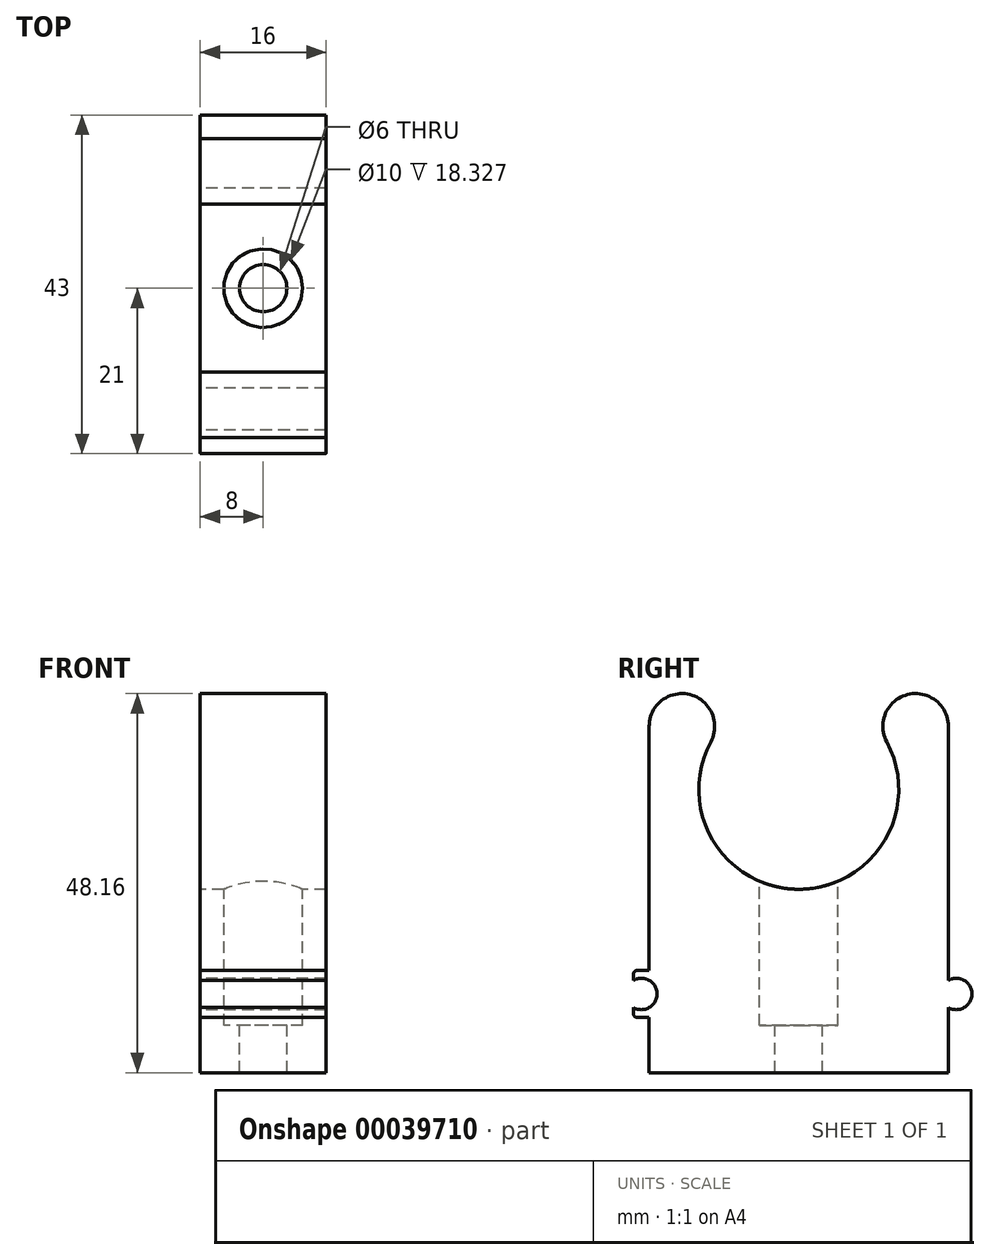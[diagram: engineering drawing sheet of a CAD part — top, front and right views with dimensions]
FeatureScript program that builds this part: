
annotation { "Feature Type Name" : "Feature", "Feature Type Description" : "" }
export const myFeature = defineFeature(function(context is Context, id is Id, definition is map)
    precondition{}
    {
        {
            var Q0;
            Q0=qCreatedBy(makeId("Right.planeOp"),FACE);
            var sketch = newSketch(context, id + "F0", { "sketchPlane" : qUnion([Q0])});
            skLineSegment(sketch, "E0", {"start": v(-19, -36) * mm, "end": v(19, -36) * mm});
            skLineSegment(sketch, "E1", {"start": v(-19, 8) * mm, "end": v(-19, -23) * mm});
            skLineSegment(sketch, "E2", {"start": v(19, -36) * mm, "end": v(19, -27.73) * mm});
            skLineSegment(sketch, "E3", {"start": v(19, -24.27) * mm, "end": v(19, -16.2) * mm});
            skLineSegment(sketch, "E4", {"start": v(19, -16.2) * mm, "end": v(19, 8) * mm});
            skArc(sketch, "E5", {"start": v(-11.18, 6.03) * mm, "mid": v(0, -12.7) * mm, "end": v(11.18, 6.03) * mm});
            skArc(sketch, "E6", {"start": v(-11.18, 6.03) * mm, "mid": v(-13.82, 12.03) * mm, "end": v(-19, 8) * mm});
            skArc(sketch, "E7", {"start": v(19, 8) * mm, "mid": v(13.82, 12.03) * mm, "end": v(11.18, 6.03) * mm});
            skArc(sketch, "E8", {"start": v(19, -27.73) * mm, "mid": v(22, -26) * mm, "end": v(19, -24.27) * mm});
            skArc(sketch, "E9", {"start": v(-21, -27.73) * mm, "mid": v(-18, -26) * mm, "end": v(-21, -24.27) * mm});
            skLineSegment(sketch, "E10", {"start": v(-19, -36) * mm, "end": v(-19, -29) * mm});
            skLineSegment(sketch, "E11", {"start": v(-19, -29) * mm, "end": v(-21, -29) * mm});
            skLineSegment(sketch, "E12", {"start": v(-19, -23) * mm, "end": v(-21, -23) * mm});
            skLineSegment(sketch, "E13", {"start": v(-21, -23) * mm, "end": v(-21, -24.27) * mm});
            skLineSegment(sketch, "E14.trimOffspring", {"start": v(-21, -27.73) * mm, "end": v(-21, -29) * mm});
            skSolve(sketch);
        }
        {
            var Q0;
            Q0=makeQuery(id+"F0.imprint","IMPRINT",FACE,{"disambiguationData":[TD([[makeQuery(id+"F0.imprint","IMPRINT",EDGE,{"derivedFrom":sQuery(id+"F0.wireOp",EDGE,"E0")}),1.0]])]});
            extrude(context, id + "F1", {"entities" : qUnion([Q0]), "depth" : 8 * mm, "hasSecondDirection" : true, "secondDirectionOppositeDirection" : true, "secondDirectionDepth" : 8 * mm});
        }
        {
            var Q0;
            Q0=qCreatedBy(makeId("Top.planeOp"),FACE);
            var sketch = newSketch(context, id + "F2", { "sketchPlane" : qUnion([Q0])});
            skPoint(sketch, "E15", {"position": v(0, 0) * mm});
            skSolve(sketch);
        }
        {
            var Q0;
            Q0=sQuery(id+"F2.wireOp",VERTEX,"E15");
            var Q1;
            Q1=makeQuery(id+"F1.opExtrude","SWEPT_BODY",BODY,{"disambiguationData":[OSD([sQuery(id+"F0.wireOp",EDGE,"E0"),sQuery(id+"F0.wireOp",EDGE,"E1"),sQuery(id+"F0.wireOp",EDGE,"19a90b0d-b803-49e8-be4d-187521ffc359"),sQuery(id+"F0.wireOp",EDGE,"1b800cd7-7c4f-49d2-8106-a57427bceeb3"),sQuery(id+"F0.wireOp",EDGE,"E2"),sQuery(id+"F0.wireOp",EDGE,"E3"),sQuery(id+"F0.wireOp",EDGE,"E4"),sQuery(id+"F0.wireOp",EDGE,"E5"),sQuery(id+"F0.wireOp",EDGE,"E6"),sQuery(id+"F0.wireOp",EDGE,"E7"),sQuery(id+"F0.wireOp",EDGE,"2815f36b-3cf0-4143-92a6-0daac1c242e2"),sQuery(id+"F0.wireOp",EDGE,"1d684afa-b3c8-4d1a-add7-a196b7715977.trimOffspring"),sQuery(id+"F0.wireOp",EDGE,"E8"),sQuery(id+"F0.wireOp",EDGE,"f289f422-6954-4b73-9159-115b672b6794.trimOffspring")])]});
            hole(context, id + "F3", {"style" : HoleStyle.C_BORE, "holeDiameter" : 6 * mm, "cBoreDiameter" : 10 * mm, "cBoreDepth" : 17.3 * mm, "endStyle" : HoleEndStyle.THROUGH, "locations" : qUnion([Q0]), "scope" : qUnion([Q1])});
        }
        {
            var Q0;
            Q0=makeQuery(id+"F1.opExtrude","SWEPT_EDGE",EDGE,{"disambiguationData":[OSD([sQuery(id+"F0.wireOp",EDGE,"E12"),sQuery(id+"F0.wireOp",EDGE,"E13")])]});
            var Q1;
            Q1=makeQuery(id+"F1.opExtrude","SWEPT_EDGE",EDGE,{"disambiguationData":[OSD([sQuery(id+"F0.wireOp",EDGE,"E11"),sQuery(id+"F0.wireOp",EDGE,"E14.trimOffspring")])]});
            fillet(context, id + "F4", {"entities" : qUnion([Q0, Q1]), "radius" : 0.5 * mm, "tangentPropagation" : true, "allowEdgeOverflow" : false});
        }
    });
